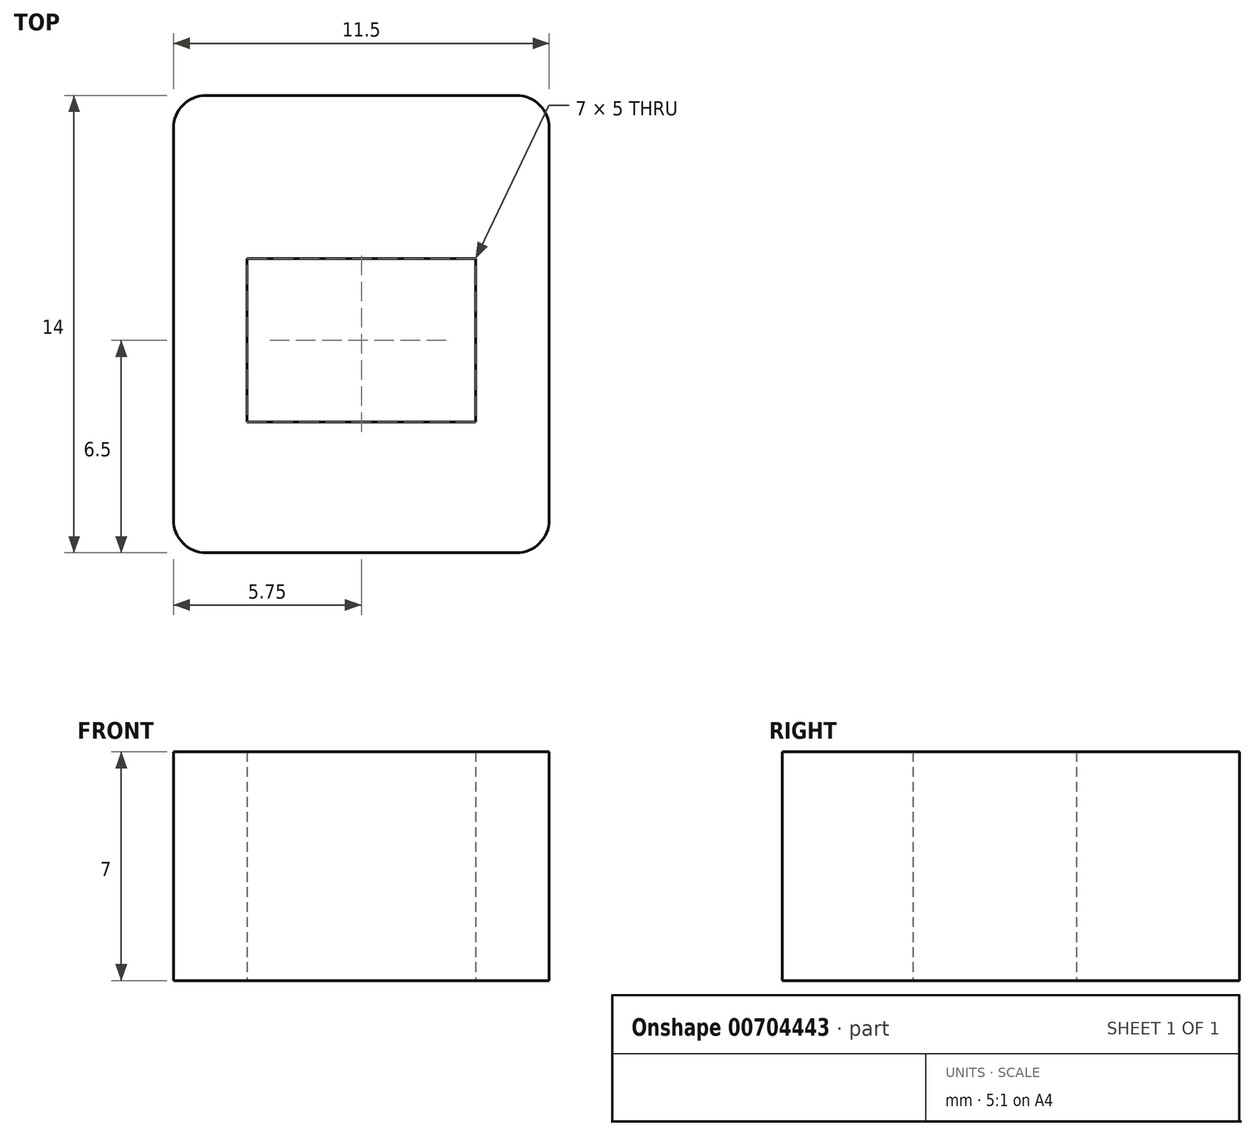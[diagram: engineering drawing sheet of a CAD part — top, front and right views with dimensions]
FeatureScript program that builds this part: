
annotation { "Feature Type Name" : "Feature", "Feature Type Description" : "" }
export const myFeature = defineFeature(function(context is Context, id is Id, definition is map)
    precondition{}
    {
        {
            var Q0;
            Q0=qCreatedBy(makeId("Top.planeOp"),FACE);
            var sketch = newSketch(context, id + "F0", { "sketchPlane" : qUnion([Q0])});
            skLineSegment(sketch, "E0.bottom", {"start": v(3.5, 2.5) * mm, "end": v(-3.5, 2.5) * mm});
            skLineSegment(sketch, "E0.top", {"start": v(3.5, -2.5) * mm, "end": v(-3.5, -2.5) * mm});
            skLineSegment(sketch, "E0.left", {"start": v(3.5, 2.5) * mm, "end": v(3.5, -2.5) * mm});
            skLineSegment(sketch, "E0.right", {"start": v(-3.5, 2.5) * mm, "end": v(-3.5, -2.5) * mm});
            skPoint(sketch, "E0.middle", {"position": v(0, 0) * mm});
            skLineSegment(sketch, "E1", {"start": v(-5.75, 7.5) * mm, "end": v(5.75, 7.5) * mm});
            skLineSegment(sketch, "E2", {"start": v(-5.75, 7.5) * mm, "end": v(-5.75, -6.5) * mm});
            skLineSegment(sketch, "E3", {"start": v(-5.75, -6.5) * mm, "end": v(5.75, -6.5) * mm});
            skLineSegment(sketch, "E4", {"start": v(5.75, -6.5) * mm, "end": v(5.75, 7.5) * mm});
            skSolve(sketch);
        }
        {
            var Q0;
            Q0=makeQuery(id+"F0.imprint","IMPRINT",FACE,{"disambiguationData":[TD([[makeQuery(id+"F0.imprint","IMPRINT",EDGE,{"derivedFrom":sQuery(id+"F0.wireOp",EDGE,"E0.bottom")}),-1.0]])]});
            extrude(context, id + "F1", {"entities" : qUnion([Q0]), "depth" : 7 * mm, "offsetDistance" : 25 * mm});
        }
        {
            var Q0;
            Q0=makeQuery(id+"F1.opExtrude","SWEPT_EDGE",EDGE,{"disambiguationData":[OSD([sQuery(id+"F0.wireOp",EDGE,"E2"),sQuery(id+"F0.wireOp",EDGE,"E3")])]});
            var Q1;
            Q1=makeQuery(id+"F1.opExtrude","SWEPT_EDGE",EDGE,{"disambiguationData":[OSD([sQuery(id+"F0.wireOp",EDGE,"E3"),sQuery(id+"F0.wireOp",EDGE,"E4")])]});
            var Q2;
            Q2=makeQuery(id+"F1.opExtrude","SWEPT_EDGE",EDGE,{"disambiguationData":[OSD([sQuery(id+"F0.wireOp",EDGE,"E1"),sQuery(id+"F0.wireOp",EDGE,"E4")])]});
            var Q3;
            Q3=makeQuery(id+"F1.opExtrude","SWEPT_EDGE",EDGE,{"disambiguationData":[OSD([sQuery(id+"F0.wireOp",EDGE,"E1"),sQuery(id+"F0.wireOp",EDGE,"E2")])]});
            fillet(context, id + "F2", {"entities" : qUnion([Q0, Q1, Q2, Q3]), "tangentPropagation" : true, "radius" : 1 * mm, "defaultsChanged" : true, "vertexSettings" : [], "allowEdgeOverflow" : false});
        }
    });
